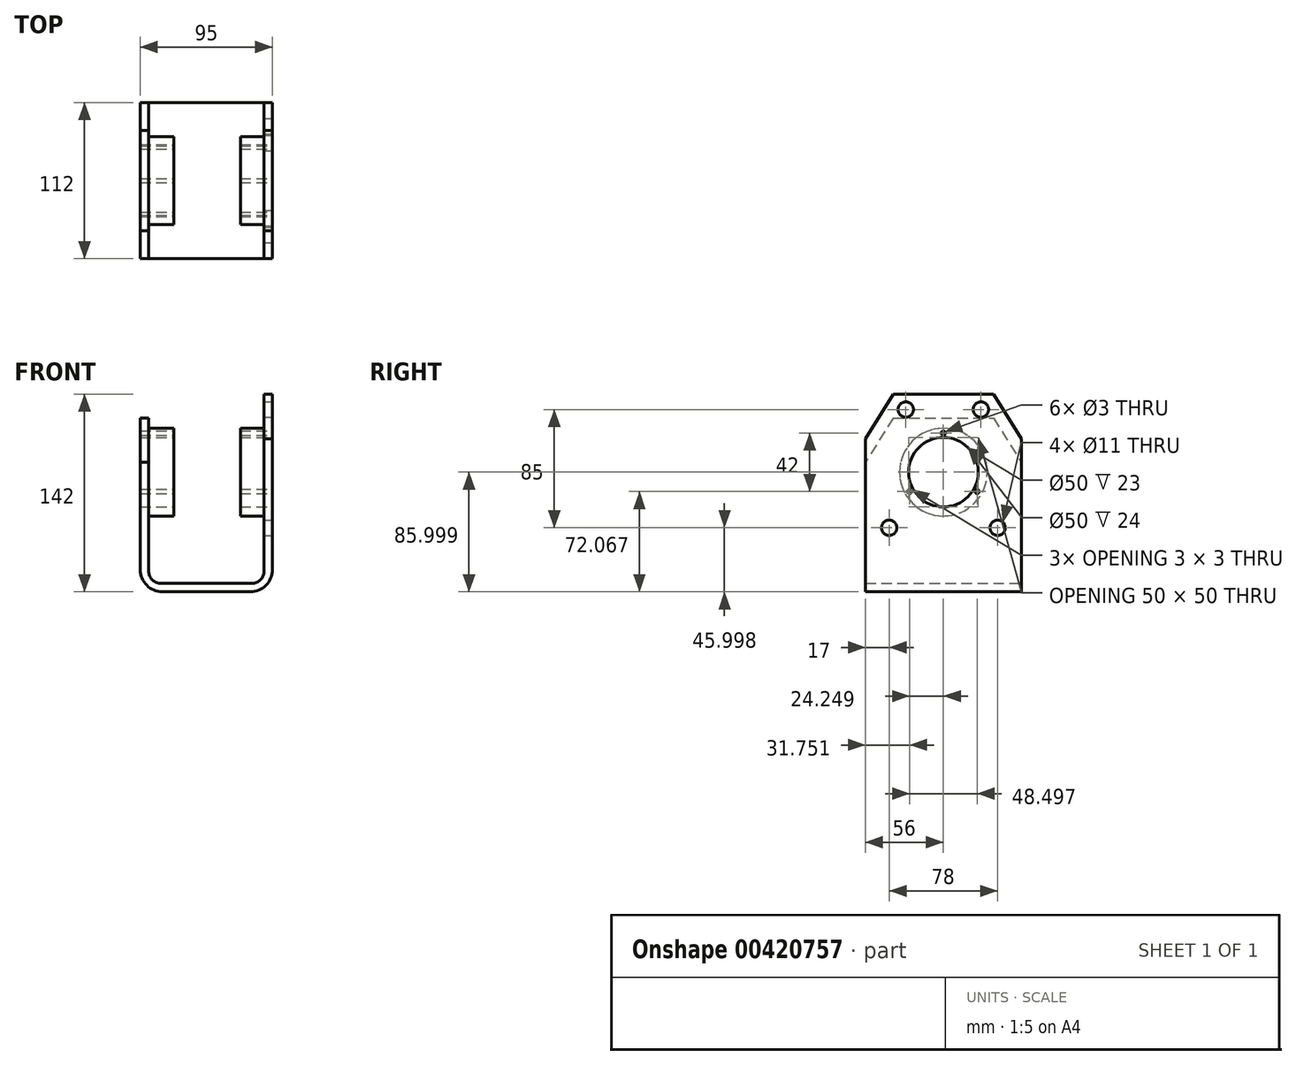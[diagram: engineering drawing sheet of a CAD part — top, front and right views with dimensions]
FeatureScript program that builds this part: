
annotation { "Feature Type Name" : "Feature", "Feature Type Description" : "" }
export const myFeature = defineFeature(function(context is Context, id is Id, definition is map)
    precondition{}
    {
        {
            var Q0;
            Q0=qCreatedBy(makeId("Front.planeOp"),FACE);
            var sketch = newSketch(context, id + "F0", { "sketchPlane" : qUnion([Q0])});
            skLineSegment(sketch, "E0.top", {"start": v(-43.8, -38.82) * mm, "end": v(19.2, -38.82) * mm});
            skLineSegment(sketch, "E0.right", {"start": v(35.2, 103.18) * mm, "end": v(35.2, -22.82) * mm});
            skLineSegment(sketch, "E1.top", {"start": v(-44.8, -32.82) * mm, "end": v(20.2, -32.82) * mm});
            skLineSegment(sketch, "E1.right", {"start": v(29.2, 103.18) * mm, "end": v(29.2, -23.82) * mm});
            skLineSegment(sketch, "E2", {"start": v(29.2, 103.18) * mm, "end": v(35.2, 103.18) * mm});
            skLineSegment(sketch, "E3.right", {"start": v(29.2, 103.18) * mm, "end": v(29.2, 87.18) * mm});
            skLineSegment(sketch, "E4", {"start": v(-53.8, -23.82) * mm, "end": v(-53.8, 86.18) * mm});
            skLineSegment(sketch, "E5", {"start": v(-53.8, 86.18) * mm, "end": v(-59.8, 86.18) * mm});
            skLineSegment(sketch, "E6", {"start": v(-59.8, 86.18) * mm, "end": v(-59.8, -22.82) * mm});
            skPoint(sketch, "E7.visualSharp", {"position": v(-53.8, -32.82) * mm});
            skArc(sketch, "E7.filletArc", {"start": v(-53.8, -23.82) * mm, "mid": v(-51.16, -30.19) * mm, "end": v(-44.8, -32.82) * mm});
            skPoint(sketch, "E8.visualSharp", {"position": v(-59.8, -38.82) * mm});
            skArc(sketch, "E8.filletArc", {"start": v(-59.8, -22.82) * mm, "mid": v(-55.1, -34.14) * mm, "end": v(-43.8, -38.82) * mm});
            skPoint(sketch, "E9.visualSharp", {"position": v(29.2, -32.82) * mm});
            skArc(sketch, "E9.filletArc", {"start": v(20.2, -32.82) * mm, "mid": v(26.57, -30.19) * mm, "end": v(29.2, -23.82) * mm});
            skPoint(sketch, "E10.visualSharp", {"position": v(35.2, -38.82) * mm});
            skArc(sketch, "E10.filletArc", {"start": v(19.2, -38.82) * mm, "mid": v(30.52, -34.14) * mm, "end": v(35.2, -22.82) * mm});
            skSolve(sketch);
        }
        {
            var Q0;
            Q0=makeQuery(id+"F0.imprint","IMPRINT",FACE,{"disambiguationData":[TD([[makeQuery(id+"F0.imprint","IMPRINT",EDGE,{"derivedFrom":sQuery(id+"F0.wireOp",EDGE,"E0.top")}),1.0]])]});
            extrude(context, id + "F1", {"entities" : qUnion([Q0]), "depth" : 112 * mm});
        }
        {
            var Q0;
            Q0=makeQuery(id+"F1.opExtrude","SWEPT_FACE",FACE,{"disambiguationData":[OSD([sQuery(id+"F0.wireOp",EDGE,"E0.right")])]});
            var sketch = newSketch(context, id + "F2", { "sketchPlane" : qUnion([Q0])});
            skCircle(sketch, "E11", {"center": v(-56, 47.18) * mm, "radius": 25 * mm});
            skCircle(sketch, "E12", {"center": v(-56, 47.18) * mm, "radius": 31.5 * mm});
            skSolve(sketch);
        }
        {
            var Q0;
            Q0=makeQuery(id+"F2.imprint","IMPRINT",FACE,{"disambiguationData":[TD([[makeQuery(id+"F2.imprint","IMPRINT",EDGE,{"derivedFrom":sQuery(id+"F2.wireOp",EDGE,"E11")}),1.0]])]});
            extrude(context, id + "F3", {"entities" : qUnion([Q0]), "operationType" : NewBodyOperationType.REMOVE, "oppositeDirection" : true, "depth" : 185 * mm});
        }
        {
            var Q0;
            Q0=makeQuery(id+"F1.opExtrude","CAP_FACE",FACE,{"disambiguationData":[OSD([sQuery(id+"F0.wireOp",EDGE,"E0.top"),sQuery(id+"F0.wireOp",EDGE,"E0.right"),sQuery(id+"F0.wireOp",EDGE,"E1.top"),sQuery(id+"F0.wireOp",EDGE,"E1.right"),sQuery(id+"F0.wireOp",EDGE,"E2"),sQuery(id+"F0.wireOp",EDGE,"E3.right"),sQuery(id+"F0.wireOp",EDGE,"E4"),sQuery(id+"F0.wireOp",EDGE,"E5"),sQuery(id+"F0.wireOp",EDGE,"E6"),sQuery(id+"F0.wireOp",EDGE,"E7.filletArc"),sQuery(id+"F0.wireOp",EDGE,"E8.filletArc"),sQuery(id+"F0.wireOp",EDGE,"E9.filletArc"),sQuery(id+"F0.wireOp",EDGE,"E10.filletArc")])],"isStart":false});
            cPlane(context, id + "F4", {"entities" : qUnion([Q0]), "cplaneType" : CPlaneType.OFFSET, "offset" : 25 * mm, "width" : 150 * mm, "height" : 150 * mm});
        }
        {
            var Q0;
            Q0=makeQuery(id+"F2.imprint","IMPRINT",FACE,{"disambiguationData":[TD([[makeQuery(id+"F2.imprint","IMPRINT",EDGE,{"derivedFrom":sQuery(id+"F2.wireOp",EDGE,"E11")}),-1.0]])]});
            extrude(context, id + "F5", {"entities" : qUnion([Q0]), "operationType" : NewBodyOperationType.REMOVE, "oppositeDirection" : true, "depth" : 184 * mm});
        }
        {
            var Q0;
            Q0=makeQuery(id+"F2.imprint","IMPRINT",FACE,{"disambiguationData":[TD([[makeQuery(id+"F2.imprint","IMPRINT",EDGE,{"derivedFrom":sQuery(id+"F2.wireOp",EDGE,"E11")}),-1.0]])]});
            extrude(context, id + "F6", {"entities" : qUnion([Q0]), "operationType" : NewBodyOperationType.ADD, "oppositeDirection" : true, "depth" : 95 * mm});
        }
        {
            var Q0;
            Q0=qCreatedBy(id+"F4.planeOp",FACE);
            var sketch = newSketch(context, id + "F7", { "sketchPlane" : qUnion([Q0])});
            skLineSegment(sketch, "E13.bottom", {"start": v(-35.8, 79.18) * mm, "end": v(12.2, 79.18) * mm});
            skLineSegment(sketch, "E13.top", {"start": v(-35.8, -20.82) * mm, "end": v(12.2, -20.82) * mm});
            skLineSegment(sketch, "E13.left", {"start": v(-35.8, 79.18) * mm, "end": v(-35.8, -20.82) * mm});
            skLineSegment(sketch, "E13.right", {"start": v(12.2, 79.18) * mm, "end": v(12.2, -20.82) * mm});
            skSolve(sketch);
        }
        {
            var Q0;
            Q0=makeQuery(id+"F7.imprint","IMPRINT",FACE,{"disambiguationData":[TD([[makeQuery(id+"F7.imprint","IMPRINT",EDGE,{"derivedFrom":sQuery(id+"F7.wireOp",EDGE,"E13.bottom")}),-1.0]])]});
            extrude(context, id + "F8", {"entities" : qUnion([Q0]), "operationType" : NewBodyOperationType.REMOVE, "oppositeDirection" : true, "depth" : 159 * mm});
        }
        {
            var Q0;
            Q0=makeQuery(id+"F2.imprint","IMPRINT",FACE,{"disambiguationData":[TD([[makeQuery(id+"F2.imprint","IMPRINT",EDGE,{"derivedFrom":sQuery(id+"F2.wireOp",EDGE,"E12")}),-1.0]])]});
            var sketch = newSketch(context, id + "F9", { "sketchPlane" : qUnion([Q0])});
            skCircle(sketch, "E14", {"center": v(-83, 92.18) * mm, "radius": 5.5 * mm});
            skCircle(sketch, "E15", {"center": v(-29, 92.18) * mm, "radius": 5.5 * mm});
            skCircle(sketch, "E16", {"center": v(-95, 7.18) * mm, "radius": 5.5 * mm});
            skCircle(sketch, "E17", {"center": v(-17, 7.18) * mm, "radius": 5.5 * mm});
            skPoint(sketch, "E18", {"position": v(-56, 47.25) * mm});
            skPoint(sketch, "E19", {"position": v(-80.25, 33.25) * mm});
            skPoint(sketch, "E20", {"position": v(-31.75, 33.25) * mm});
            skPoint(sketch, "E21", {"position": v(-56, 75.25) * mm});
            skCircle(sketch, "E22", {"center": v(-80.25, 33.25) * mm, "radius": 1.5 * mm});
            skCircle(sketch, "E23", {"center": v(-56, 75.25) * mm, "radius": 1.5 * mm});
            skCircle(sketch, "E24", {"center": v(-31.75, 33.25) * mm, "radius": 1.5 * mm});
            skLineSegment(sketch, "E25", {"start": v(-56, 75.25) * mm, "end": v(-56, 47.25) * mm});
            skSolve(sketch);
        }
        {
            var Q0;
            Q0=makeQuery(id+"F9.imprint","IMPRINT",FACE,{"disambiguationData":[TD([[makeQuery(id+"F9.imprint","IMPRINT",EDGE,{"derivedFrom":sQuery(id+"F9.wireOp",EDGE,"E14")}),1.0]])]});
            var Q1;
            Q1=makeQuery(id+"F9.imprint","IMPRINT",FACE,{"disambiguationData":[TD([[makeQuery(id+"F9.imprint","IMPRINT",EDGE,{"derivedFrom":sQuery(id+"F9.wireOp",EDGE,"E15")}),1.0]])]});
            var Q2;
            Q2=makeQuery(id+"F9.imprint","IMPRINT",FACE,{"disambiguationData":[TD([[makeQuery(id+"F9.imprint","IMPRINT",EDGE,{"derivedFrom":sQuery(id+"F9.wireOp",EDGE,"E16")}),1.0]])]});
            var Q3;
            Q3=makeQuery(id+"F9.imprint","IMPRINT",FACE,{"disambiguationData":[TD([[makeQuery(id+"F9.imprint","IMPRINT",EDGE,{"derivedFrom":sQuery(id+"F9.wireOp",EDGE,"E17")}),1.0]])]});
            extrude(context, id + "F10", {"entities" : qUnion([Q0, Q1, Q2, Q3]), "operationType" : NewBodyOperationType.REMOVE, "oppositeDirection" : true, "depth" : 39.1 * mm});
        }
        {
            var Q0;
            Q0=makeQuery(id+"F9.imprint","IMPRINT",FACE,{"disambiguationData":[TD([[makeQuery(id+"F9.imprint","IMPRINT",EDGE,{"derivedFrom":sQuery(id+"F9.wireOp",EDGE,"E24")}),1.0]])]});
            var Q1;
            Q1=makeQuery(id+"F9.imprint","IMPRINT",FACE,{"disambiguationData":[TD([[makeQuery(id+"F9.imprint","IMPRINT",EDGE,{"derivedFrom":sQuery(id+"F9.wireOp",EDGE,"E22")}),1.0]])]});
            var Q2;
            Q2=makeQuery(id+"F9.imprint","IMPRINT",FACE,{"disambiguationData":[TD([[makeQuery(id+"F9.imprint","IMPRINT",EDGE,{"derivedFrom":sQuery(id+"F9.wireOp",EDGE,"E23")}),1.0]])]});
            extrude(context, id + "F11", {"entities" : qUnion([Q0, Q1, Q2]), "operationType" : NewBodyOperationType.REMOVE, "oppositeDirection" : true, "depth" : 154.4 * mm});
        }
        {
            var Q0;
            Q0=makeQuery(id+"F1.opExtrude","CAP_EDGE",EDGE,{"disambiguationData":[OSD([sQuery(id+"F0.wireOp",EDGE,"E5")])],"isStart":true});
            var Q1;
            Q1=makeQuery(id+"F1.opExtrude","CAP_EDGE",EDGE,{"disambiguationData":[OSD([sQuery(id+"F0.wireOp",EDGE,"E2")])],"isStart":true});
            var Q2;
            Q2=makeQuery(id+"F1.opExtrude","CAP_EDGE",EDGE,{"disambiguationData":[OSD([sQuery(id+"F0.wireOp",EDGE,"E5")])],"isStart":false});
            var Q3;
            Q3=makeQuery(id+"F1.opExtrude","CAP_EDGE",EDGE,{"disambiguationData":[OSD([sQuery(id+"F0.wireOp",EDGE,"E2")])],"isStart":false});
            chamfer(context, id + "F12", {"entities" : qUnion([Q0, Q1, Q2, Q3]), "chamferType" : ChamferType.TWO_OFFSETS, "width1" : 20 * mm, "oppositeDirection" : false, "width2" : 32 * mm, "tangentPropagation" : true});
        }
    });
